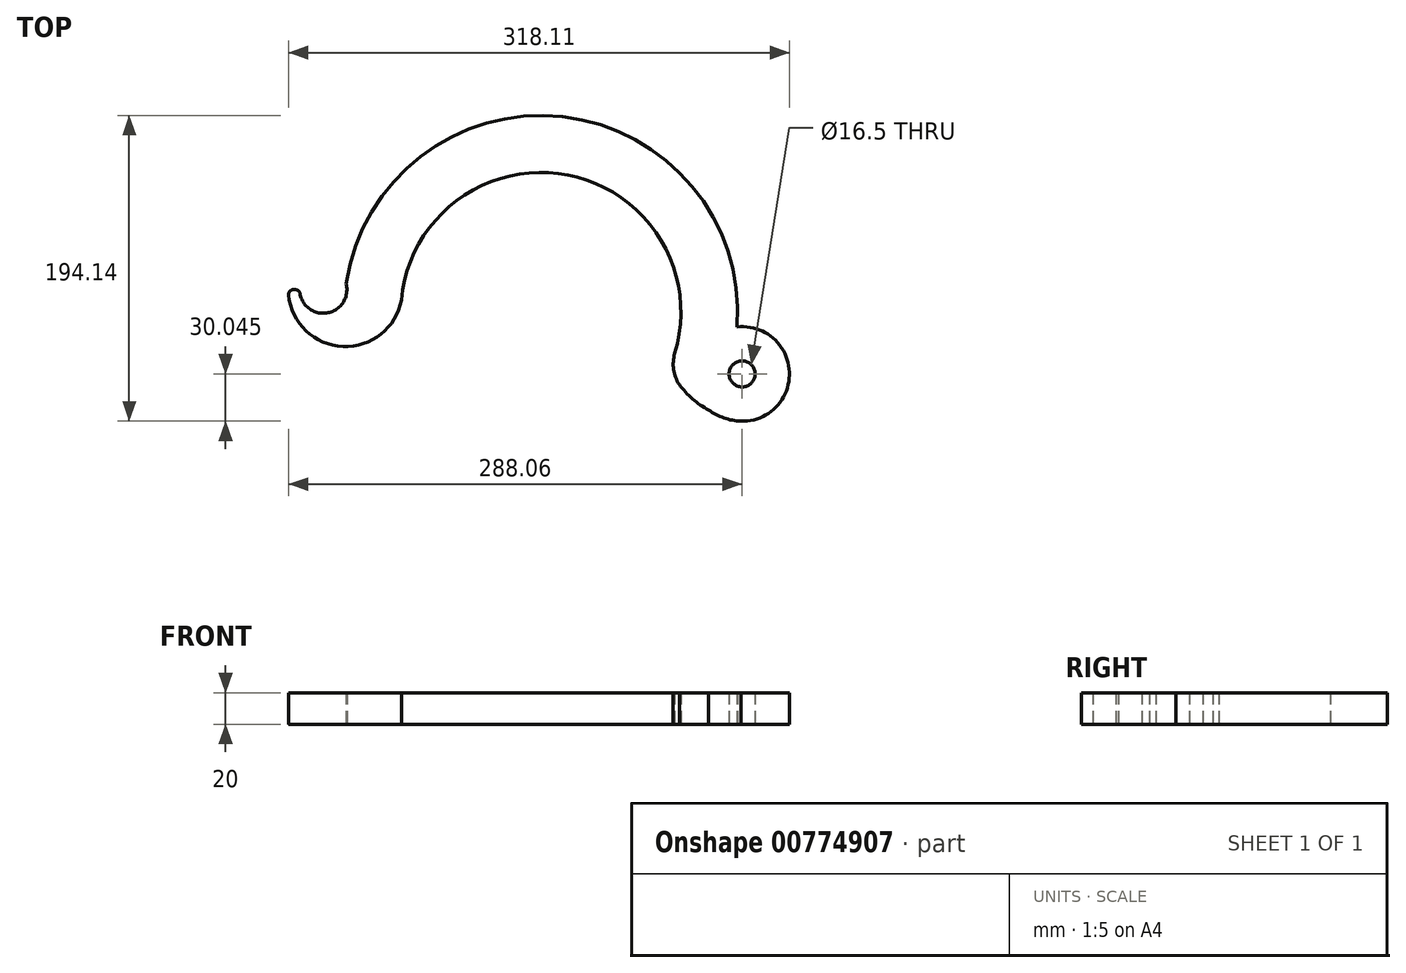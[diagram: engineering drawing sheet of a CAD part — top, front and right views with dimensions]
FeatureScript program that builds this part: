
annotation { "Feature Type Name" : "Feature", "Feature Type Description" : "" }
export const myFeature = defineFeature(function(context is Context, id is Id, definition is map)
    precondition{}
    {
        {
            var Q0;
            Q0=qCreatedBy(makeId("Top.planeOp"),FACE);
            var sketch = newSketch(context, id + "F0", { "sketchPlane" : qUnion([Q0])});
            skArc(sketch, "E0", {"start": v(-160.36, 14.45) * mm, "mid": v(-127.4, -21.6) * mm, "end": v(-88.54, 8) * mm});
            skLineSegment(sketch, "E1.trimOffspring", {"start": v(-153.21, 14.45) * mm, "end": v(-160.36, 14.45) * mm, "construction": true});
            skLineSegment(sketch, "E2", {"start": v(-160.36, 14.45) * mm, "end": v(-153.21, 14.45) * mm});
            skCircle(sketch, "E3", {"center": v(127.83, -39.1) * mm, "radius": 8.25 * mm});
            skArc(sketch, "E4.trimOffspring", {"start": v(85.01, -26) * mm, "mid": v(86.08, -22.2) * mm, "end": v(86.98, -18.35) * mm});
            skArc(sketch, "E5.trimOffspring", {"start": v(124.66, -9.21) * mm, "mid": v(13.7, 124.25) * mm, "end": v(-123.68, 18.15) * mm});
            skArc(sketch, "E6.trimOffspring", {"start": v(86.98, -18.35) * mm, "mid": v(13.2, 87.91) * mm, "end": v(-88.54, 8) * mm});
            skLineSegment(sketch, "E7", {"start": v(0, 0) * mm, "end": v(0, 88.9) * mm, "construction": true});
            skLineSegment(sketch, "E8", {"start": v(0, 0) * mm, "end": v(127.83, -39.1) * mm, "construction": true});
            skArc(sketch, "E9", {"start": v(85.01, -26) * mm, "mid": v(84.3, -36.23) * mm, "end": v(87.89, -45.83) * mm});
            skArc(sketch, "E10", {"start": v(127.1, -69.13) * mm, "mid": v(157.85, -37.88) * mm, "end": v(124.66, -9.21) * mm});
            skArc(sketch, "E11", {"start": v(87.89, -45.83) * mm, "mid": v(96.34, -54.89) * mm, "end": v(106.48, -62) * mm});
            skArc(sketch, "E12", {"start": v(106.48, -62) * mm, "mid": v(116.27, -67.06) * mm, "end": v(127.1, -69.13) * mm});
            skArc(sketch, "E13", {"start": v(60.62, -35) * mm, "mid": v(61.37, -33.66) * mm, "end": v(62.1, -32.3) * mm});
            skArc(sketch, "E14", {"start": v(-67.74, -17.64) * mm, "mid": v(-61.83, -32.8) * mm, "end": v(-52.59, -46.2) * mm});
            skLineSegment(sketch, "E15", {"start": v(0, 0) * mm, "end": v(0, -70) * mm});
            skLineSegment(sketch, "E16", {"start": v(0, 0) * mm, "end": v(0, -70) * mm, "construction": true});
            skLineSegment(sketch, "E17", {"start": v(0, 0) * mm, "end": v(154.45, -47.24) * mm, "construction": true});
            skLineSegment(sketch, "E18", {"start": v(-67.74, -76.62) * mm, "end": v(-67.74, -76.62) * mm});
            skArc(sketch, "E19", {"start": v(89.08, -7.13) * mm, "mid": v(88.84, -7.23) * mm, "end": v(88.6, -7.34) * mm});
            skArc(sketch, "E20", {"start": v(82.92, 11.54) * mm, "mid": v(82.36, 12.03) * mm, "end": v(81.78, 12.5) * mm});
            skArc(sketch, "E21", {"start": v(124.77, -7.66) * mm, "mid": v(124.77, -7.66) * mm, "end": v(124.77, -7.66) * mm});
            skArc(sketch, "E22.trimOffspring", {"start": v(66.94, -20.47) * mm, "mid": v(1.47, 69.98) * mm, "end": v(-67.74, -17.64) * mm, "construction": true});
            skArc(sketch, "E23", {"start": v(-153.21, 14.45) * mm, "mid": v(-136.35, -0.43) * mm, "end": v(-123.68, 18.15) * mm});
            skLineSegment(sketch, "E24", {"start": v(127.83, -39.1) * mm, "end": v(127.83, -30.84) * mm});
            skLineSegment(sketch, "E25", {"start": v(127.83, -39.1) * mm, "end": v(127.83, -47.34) * mm});
            skLineSegment(sketch, "E26", {"start": v(127.83, -39.1) * mm, "end": v(119.58, -39.1) * mm});
            skLineSegment(sketch, "E27", {"start": v(127.83, -39.1) * mm, "end": v(136.08, -39.1) * mm});
            skLineSegment(sketch, "E28", {"start": v(112.53, -83.56) * mm, "end": v(12.53, -83.56) * mm});
            skLineSegment(sketch, "E29", {"start": v(12.53, -83.56) * mm, "end": v(12.53, -73.56) * mm});
            skLineSegment(sketch, "E30", {"start": v(112.53, -83.56) * mm, "end": v(112.53, -73.56) * mm});
            skLineSegment(sketch, "E31", {"start": v(127.83, -39.1) * mm, "end": v(-160.36, 14.45) * mm, "construction": true});
            skSolve(sketch);
        }
        {
            var Q0;
            Q0=makeQuery(id+"F0.imprint","IMPRINT",FACE,{"disambiguationData":[TD([[makeQuery(id+"F0.imprint","IMPRINT",EDGE,{"derivedFrom":sQuery(id+"F0.wireOp",EDGE,"E0")}),1.0]])]});
            extrude(context, id + "F1", {"entities" : qUnion([Q0]), "depth" : 20 * mm, "offsetDistance" : 25 * mm});
        }
        {
            var Q0;
            Q0=makeQuery(id+"F1.opExtrude","SWEPT_EDGE",EDGE,{"disambiguationData":[OSD([sQuery(id+"F0.wireOp",EDGE,"E0"),sQuery(id+"F0.wireOp",EDGE,"E2")])]});
            var Q1;
            Q1=makeQuery(id+"F1.opExtrude","SWEPT_EDGE",EDGE,{"disambiguationData":[OSD([sQuery(id+"F0.wireOp",EDGE,"0sHbk03A-FTYv-Vbhb-L70f-OfD4ufr7hiPc"),sQuery(id+"F0.wireOp",EDGE,"qpgQZdVH-zJn7-8eAc-3cFM-GKPumjwzCIUO")])]});
            var Q2;
            Q2=makeQuery(id+"F1.opExtrude","SWEPT_EDGE",EDGE,{"disambiguationData":[OSD([sQuery(id+"F0.wireOp",EDGE,"0sHbk03A-FTYv-Vbhb-L70f-OfD4ufr7hiPc"),sQuery(id+"F0.wireOp",EDGE,"E2")])]});
            fillet(context, id + "F2", {"entities" : qUnion([Q0, Q1, Q2]), "radius" : 3 * mm, "tangentPropagation" : true, "allowEdgeOverflow" : false});
        }
    });
